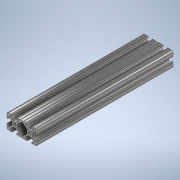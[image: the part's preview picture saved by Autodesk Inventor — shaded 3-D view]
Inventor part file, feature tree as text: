
AUTODESK INVENTOR PART (.ipt)
format: ipt  version: 2020 (Build 240168000, 168)  size: 344,576 bytes
history: native  units: in
note: dims shown in document units (in); Inventor stores cm internally (conversion verified against a paired STEP export)
features: sketch x2, extrude x1
ambient origin geometry x8: Origin, YZ Plane, XZ Plane, XY Plane, X Axis, Y Axis, Z Axis, Center Point
bodies: Solid1 (feature_tree)
feature tree (3):
  extrude  "Extrusion1"  [1 undecoded]
  sketch  "Sketch2"
  sketch  "Sketch1"  dims[d0=9.0in d1=0.0in]
note: 1 required parameter value undecoded (feature->parameter linkage not recoverable at this tier; creation-order binding heuristic only, values carry confidence <= 0.55)
